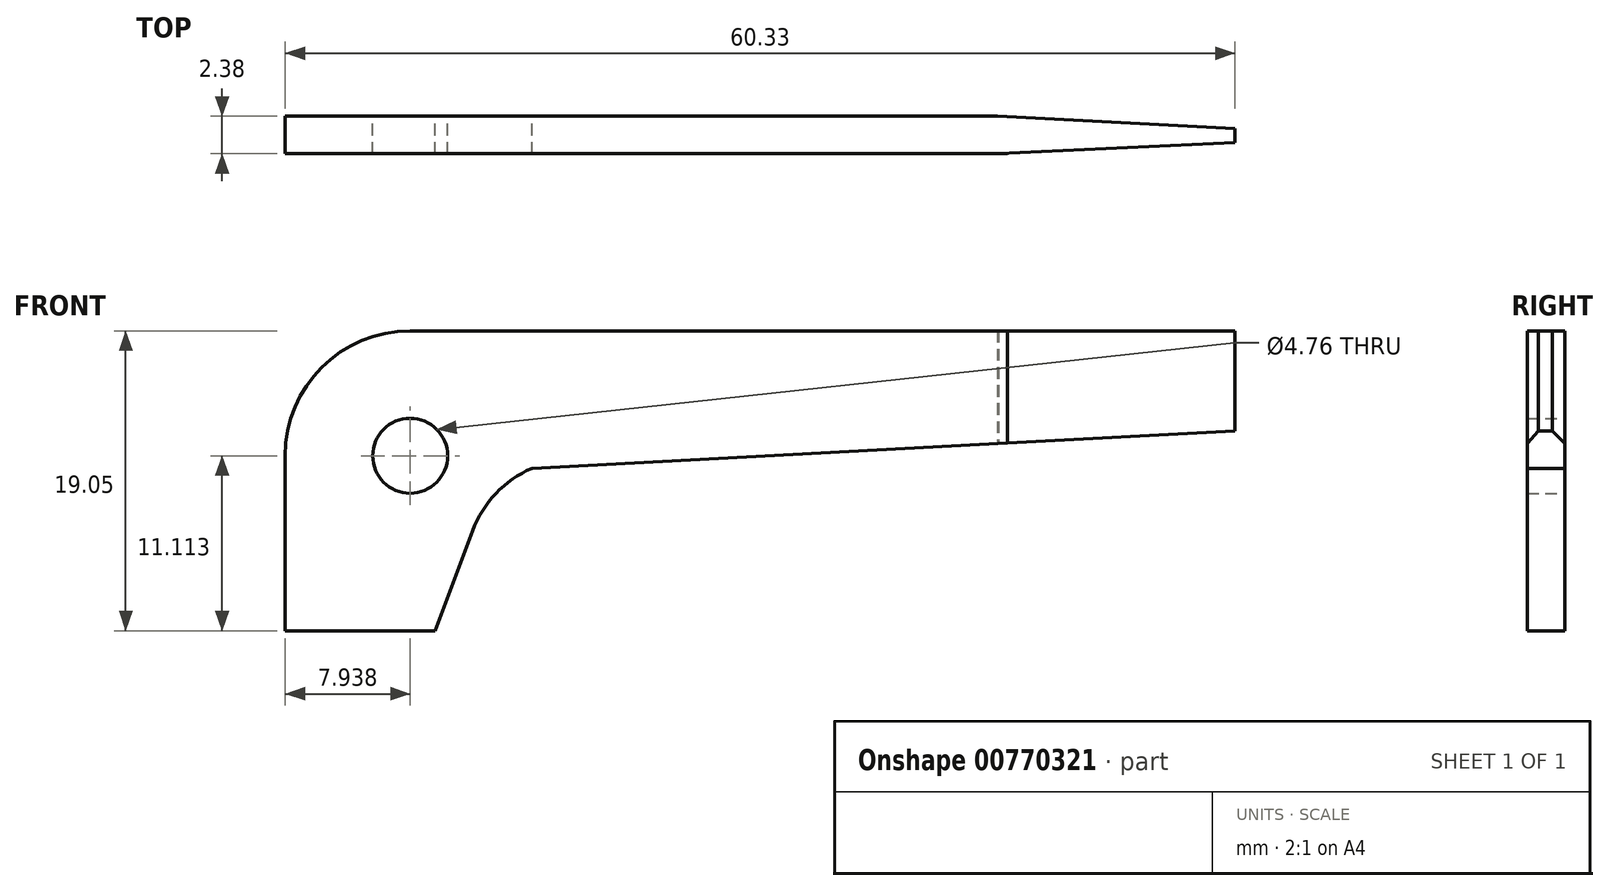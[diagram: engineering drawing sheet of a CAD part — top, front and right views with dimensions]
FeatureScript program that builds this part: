
annotation { "Feature Type Name" : "Feature", "Feature Type Description" : "" }
export const myFeature = defineFeature(function(context is Context, id is Id, definition is map)
    precondition{}
    {
        {
            var Q0;
            Q0=qCreatedBy(makeId("Front.planeOp"),FACE);
            var sketch = newSketch(context, id + "F0", { "sketchPlane" : qUnion([Q0])});
            skLineSegment(sketch, "E0.top", {"start": v(7.94, 19.05) * mm, "end": v(60.33, 19.05) * mm});
            skLineSegment(sketch, "E0.left", {"start": v(0, 0) * mm, "end": v(0, 11.11) * mm});
            skLineSegment(sketch, "E1", {"start": v(9.52, 0) * mm, "end": v(11.9, 6.35) * mm});
            skLineSegment(sketch, "E2", {"start": v(60.33, 12.7) * mm, "end": v(15.66, 10.31) * mm});
            skLineSegment(sketch, "E3", {"start": v(60.33, 19.05) * mm, "end": v(60.33, 12.7) * mm});
            skArc(sketch, "E4", {"start": v(15.66, 10.31) * mm, "mid": v(13.38, 8.71) * mm, "end": v(11.9, 6.35) * mm});
            skPoint(sketch, "E5.visualSharp", {"position": v(0, 19.05) * mm});
            skArc(sketch, "E5.filletArc", {"start": v(7.94, 19.05) * mm, "mid": v(2.32, 16.73) * mm, "end": v(0, 11.11) * mm});
            skLineSegment(sketch, "E6", {"start": v(0, 0) * mm, "end": v(9.52, 0) * mm});
            skSolve(sketch);
        }
        {
            var Q0;
            Q0 = qSketchRegion(id + "F0", true);
            var Q1;
            Q1=makeQuery(id+"F0.imprint","IMPRINT",FACE,{"disambiguationData":[TD([[makeQuery(id+"F0.imprint","IMPRINT",EDGE,{"derivedFrom":sQuery(id+"F0.wireOp",EDGE,"E0.top")}),-1.0]])]});
            extrude(context, id + "F1", {"entities" : qUnion([Q0, Q1]), "depth" : 2.38 * mm, "offsetDistance" : 25.4 * mm});
        }
        {
            var Q0;
            Q0=qCreatedBy(makeId("Front.planeOp"),FACE);
            var sketch = newSketch(context, id + "F2", { "sketchPlane" : qUnion([Q0])});
            skCircle(sketch, "E7", {"center": v(7.94, 11.11) * mm, "radius": 2.38 * mm});
            skSolve(sketch);
        }
        {
            var Q0;
            Q0 = qSketchRegion(id + "F2", true);
            extrude(context, id + "F3", {"entities" : qUnion([Q0]), "operationType" : NewBodyOperationType.REMOVE, "depth" : 25.4 * mm, "offsetDistance" : 25.4 * mm});
        }
        {
            var Q0;
            Q0=qCreatedBy(makeId("Top.planeOp"),FACE);
            var sketch = newSketch(context, id + "F4", { "sketchPlane" : qUnion([Q0])});
            skLineSegment(sketch, "E8", {"start": v(45.24, 0) * mm, "end": v(60.33, -0.8) * mm});
            skLineSegment(sketch, "E9", {"start": v(60.33, -0.8) * mm, "end": v(60.33, 0) * mm});
            skLineSegment(sketch, "E10", {"start": v(60.33, 0) * mm, "end": v(45.24, 0) * mm});
            skLineSegment(sketch, "E11", {"start": v(45.3, -2.38) * mm, "end": v(60.35, -1.66) * mm});
            skLineSegment(sketch, "E12", {"start": v(60.35, -1.66) * mm, "end": v(60.38, -2.46) * mm});
            skLineSegment(sketch, "E13", {"start": v(60.38, -2.46) * mm, "end": v(45.3, -2.38) * mm});
            skSolve(sketch);
        }
        {
            var Q0;
            Q0 = qSketchRegion(id + "F4", true);
            extrude(context, id + "F5", {"entities" : qUnion([Q0]), "operationType" : NewBodyOperationType.REMOVE, "endBound" : BoundingType.THROUGH_ALL, "depth" : 25.4 * mm, "offsetDistance" : 25.4 * mm});
        }
    });
